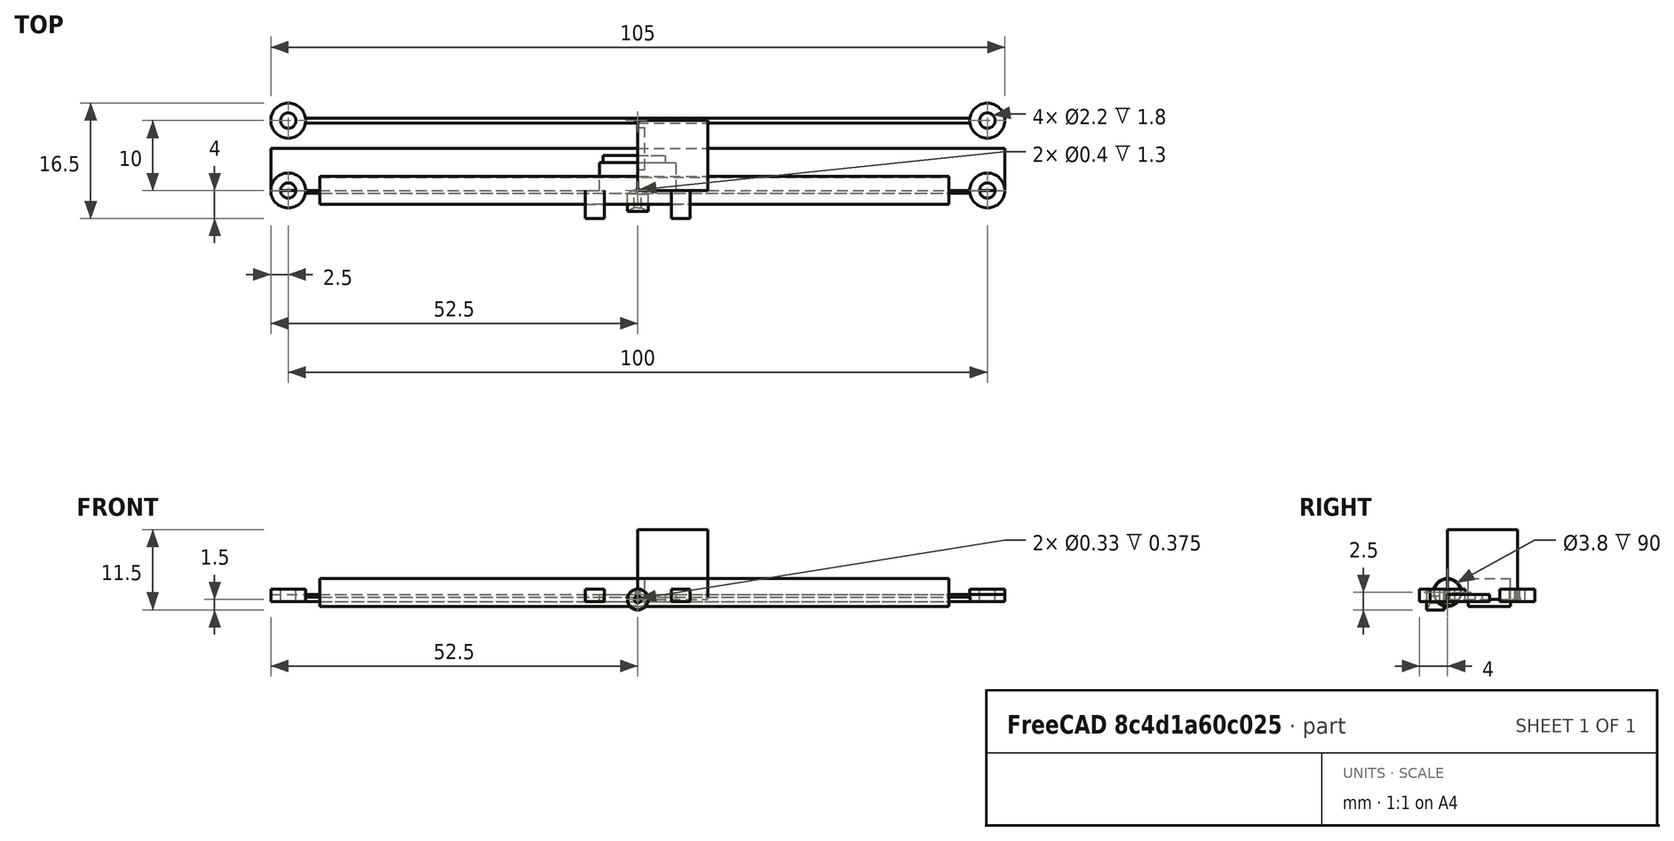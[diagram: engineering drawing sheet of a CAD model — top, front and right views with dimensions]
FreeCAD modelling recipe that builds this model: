
FCSTD DOCUMENT  (FreeCAD 0.18R16033 (Git))
Label: bowtie_prototype_1_looong
License: All rights reserved
LicenseURL: http://en.wikipedia.org/wiki/All_rights_reserved
objects: Part::Cylinder×11, Part::Box×8, Part::MultiFuse×3, Part::Cut×3, Part::Feature×2, Spreadsheet::Sheet×1, App::Part×1
note: 27 computed .brp shape members not serialized (recipe doc carries the construction recipe); baked Part::Feature solids carry a one-line shape summary decoded from their .brp

FEATURE [Part::Cylinder] Cylinder138  label="BowTieInjectorWire"
  Angle = 360
  AttacherType = Attacher::AttachEngine3D
  Height = 8
  Placement = pos=(0,0,0) rot=(-1,0,0;1.5708rad)
  Radius = 0.165
  expr: Radius = 0.33 / 2
FEATURE [Part::Cylinder] Cylinder136  label="BowTieNozzle"
  Angle = 360
  AttacherType = Attacher::AttachEngine3D
  Height = 9
  Radius = 0.2
FEATURE [Part::Cylinder] Cylinder  label="MountingHole1"
  Angle = 360
  AttacherType = Attacher::AttachEngine3D
  Height = 4
  Placement = pos=(-50,0,-1) rot=(0,0,1;0rad)
  Radius = 1.1
  expr: Placement.Base.x = -Sizes.STRIP_LENGTH / 2
  expr: Radius = Sizes.MOUNTING_ID / 2
FEATURE [Part::Box] Box  label="Strip"
  AttacherType = Attacher::AttachEngine3D
  Height = 0.6
  Length = 100
  Placement = pos=(-50,-0.375,-0.3) rot=(0,0,1;0rad)
  Width = 0.75
  expr: Width = Sizes.STRIP_WIDTH
  expr: Placement.Base.y = -Sizes.STRIP_WIDTH / 2
  expr: Length = Sizes.STRIP_LENGTH
  expr: Placement.Base.x = -Sizes.STRIP_LENGTH / 2
  expr: Height = Sizes.STRIP_HEIGHT
  expr: Placement.Base.z = -Sizes.STRIP_HEIGHT / 2
FEATURE [Spreadsheet::Sheet] Spreadsheet  label="Sizes"
  cells = A1=Strip height; B1(STRIP_HEIGHT)=0.6; A2=Strip length; B2(STRIP_LENGTH)=100; A3=strip width; B3(STRIP_WIDTH)=0.75; A4=Injection width; B4(INJECTION_WIDTH)=1.5; A5=Injection length; B5(INJECTION_LENGTH)=1.5; A6=Mounting hole ID; B6(MOUNTING_ID)=2.2; A7=Nozzle ID; B7(NOZZLE_ID)=0.4; A8=Nozzle OD; B8(NOZZLE_OD)=0.7; A9=Mounting hole OD; B9(MOUNTING_OD)=5; A10=Nozzle height; B10(NOZZLE_HEIGHT)=1; A11=Mounting hole height; B11(MOUNTING_HEIGHT)=1.8
FEATURE [Part::Cylinder] Cylinder139  label="MountingHole2"
  Angle = 360
  AttacherType = Attacher::AttachEngine3D
  Height = 4
  Placement = pos=(50,0,-1) rot=(0,0,1;0rad)
  Radius = 1.1
  expr: Placement.Base.x = Sizes.STRIP_LENGTH / 2
  expr: Radius = Sizes.MOUNTING_ID / 2
FEATURE [Part::Cylinder] Cylinder140  label="Nozzle_OD"
  Angle = 360
  AttacherType = Attacher::AttachEngine3D
  Height = 1
  Placement = pos=(0,0,0.3) rot=(0,0,1;0rad)
  Radius = 0.35
  expr: Placement.Base.z = Sizes.STRIP_HEIGHT / 2
  expr: Height = Sizes.NOZZLE_HEIGHT
  expr: Radius = Sizes.NOZZLE_OD / 2
FEATURE [Part::Cylinder] Cylinder141  label="MountingHoleOD"
  Angle = 360
  AttacherType = Attacher::AttachEngine3D
  Height = 1.8
  Placement = pos=(-50,0,-0.3) rot=(0,0,1;0rad)
  Radius = 2.5
  expr: Radius = Sizes.MOUNTING_OD / 2
  expr: Placement.Base.z = -Sizes.STRIP_HEIGHT / 2
  expr: Height = Sizes.MOUNTING_HEIGHT
  expr: Placement.Base.x = -Sizes.STRIP_LENGTH / 2
FEATURE [Part::Cylinder] Cylinder142  label="MountingHoleOD001"
  Angle = 360
  AttacherType = Attacher::AttachEngine3D
  Height = 1.8
  Placement = pos=(50,0,-0.3) rot=(0,0,1;0rad)
  Radius = 2.5
  expr: Placement.Base.z = -Sizes.STRIP_HEIGHT / 2
  expr: Height = Sizes.MOUNTING_HEIGHT
  expr: Placement.Base.x = Sizes.STRIP_LENGTH / 2
  expr: Radius = Sizes.MOUNTING_OD / 2
FEATURE [Part::MultiFuse] Fusion
  Shapes = -> [Box,Cylinder142,Cylinder141,Cylinder140]
FEATURE [Part::MultiFuse] Fusion001
  Shapes = -> [Cylinder138,Cylinder136,Cylinder,Cylinder139]
FEATURE [Part::Feature] Part__Feature  label="1"
  shape: bbox 5.8 x 3 x 3.036 mm, 8 faces (baked)
FEATURE [App::Part] CER_4  label="CER-4"
  Group = -> [Part__Feature]
  Origin = -> Origin
  Placement = pos=(-5,0,0) rot=(1,0,0;1.5708rad)
FEATURE [Part::Box] Box001  label="Support"
  AttacherType = Attacher::AttachEngine3D
  Height = 1
  Length = 105
  Placement = pos=(-52.5,0,-0.3) rot=(0,0,1;0rad)
  Width = 6
  expr: Placement.Base.x = -(Sizes.STRIP_LENGTH + Sizes.MOUNTING_OD) / 2
  expr: Length = Sizes.STRIP_LENGTH + Sizes.MOUNTING_OD
FEATURE [Part::Box] Box002  label="SupportSubtract"
  AttacherType = Attacher::AttachEngine3D
  Height = 1
  Length = 11
  Placement = pos=(-5.5,0,-0.3) rot=(0,0,1;0rad)
  Width = 4
FEATURE [Part::Cut] Cut  label="Support001"
  Base = -> Box001
  Tool = -> Box002
FEATURE [Part::Box] Box003  label="Cube"
  AttacherType = Attacher::AttachEngine3D
  Height = 1.8
  Length = 2.7
  Placement = pos=(4.8,-4,-0.3) rot=(0,0,1;0rad)
  Width = 4
FEATURE [Part::Box] Box004  label="Cube001"
  AttacherType = Attacher::AttachEngine3D
  Height = 1.8
  Length = 2.7
  Placement = pos=(-7.5,-4,-0.3) rot=(0,0,1;0rad)
  Width = 4
FEATURE [Part::Cylinder] Cylinder143  label="Cylinder"
  Angle = 360
  AttacherType = Attacher::AttachEngine3D
  Height = 10
  Placement = pos=(-6.3,-2.8,-1) rot=(0,0,1;0rad)
  Radius = 0.8
  expr: Radius = 1.6 / 2
FEATURE [Part::Cylinder] Cylinder144  label="Cylinder001"
  Angle = 360
  AttacherType = Attacher::AttachEngine3D
  Height = 10
  Placement = pos=(6.3,-2.8,-1) rot=(0,0,1;0rad)
  Radius = 0.8
  expr: Radius = 1.6 / 2
FEATURE [Part::MultiFuse] Fusion003
  Shapes = -> [Cylinder143,Cylinder144,Fusion001]
FEATURE [Part::Box] Box005  label="Cube002"
  AttacherType = Attacher::AttachEngine3D
  Height = 1
  Length = 9
  Placement = pos=(-5,4,-0.3) rot=(0,0,1;0rad)
  Width = 1
FEATURE [Part::Box] Box006  label="Cube003"
  AttacherType = Attacher::AttachEngine3D
  Height = 4
  Length = 1
  Placement = pos=(0,3,-1) rot=(0,0,1;0rad)
  Width = 6
FEATURE [Part::Cylinder] Cylinder145  label="Cylinder002"
  Angle = 360
  AttacherType = Attacher::AttachEngine3D
  Height = 90
  Placement = pos=(-2.5,0,1) rot=(0,1,0;1.5708rad)
  Radius = 2
FEATURE [Part::Cylinder] Cylinder146  label="Cylinder003"
  Angle = 360
  AttacherType = Attacher::AttachEngine3D
  Height = 100
  Placement = pos=(-2.5,0,1) rot=(0,1,0;1.5708rad)
  Radius = 1.9
FEATURE [Part::Cut] Cut003
  Base = -> Cylinder145
  Placement = pos=(-43,0,0) rot=(0,0,1;0rad)
  Tool = -> Cylinder146
FEATURE [Part::Cut] Cut004
  Base = -> Fusion
  Placement = pos=(0,10,0) rot=(0,0,1;0rad)
  Tool = -> Fusion003
FEATURE [Part::Feature] Cut004001  label="Cut005"
  shape: bbox 105 x 5 x 1.8 mm, 20 faces (baked)
FEATURE [Part::Box] Box007  label="Cube004"
  AttacherType = Attacher::AttachEngine3D
  Height = 10
  Length = 10
  Width = 10
